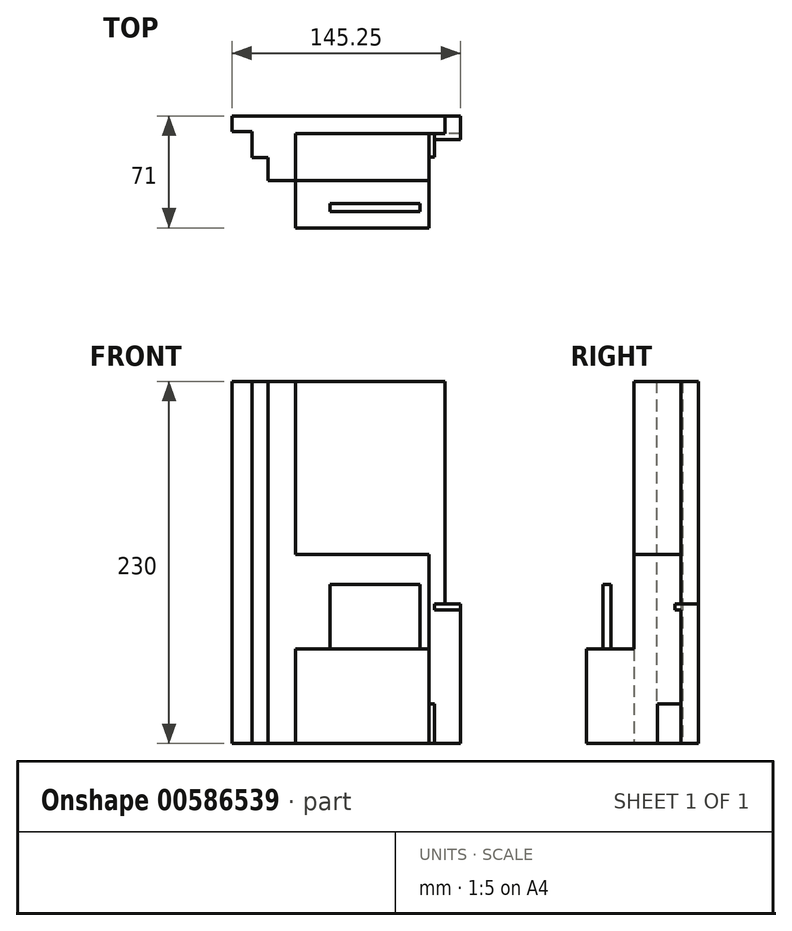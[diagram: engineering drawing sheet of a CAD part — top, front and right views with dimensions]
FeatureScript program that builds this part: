
annotation { "Feature Type Name" : "Feature", "Feature Type Description" : "" }
export const myFeature = defineFeature(function(context is Context, id is Id, definition is map)
    precondition{}
    {
        {
            var Q0;
            Q0=qCreatedBy(makeId("Top.planeOp"),FACE);
            var sketch = newSketch(context, id + "F0", { "sketchPlane" : qUnion([Q0])});
            skLineSegment(sketch, "E0", {"start": v(0, 0) * mm, "end": v(0, -30) * mm});
            skLineSegment(sketch, "E1", {"start": v(0, -30) * mm, "end": v(-17.5, -30) * mm});
            skLineSegment(sketch, "E2", {"start": v(-17.5, -30) * mm, "end": v(-17.5, -15.5) * mm});
            skLineSegment(sketch, "E3", {"start": v(-17.5, -15.5) * mm, "end": v(-27.5, -15.5) * mm});
            skLineSegment(sketch, "E4", {"start": v(-27.5, -15.5) * mm, "end": v(-27.5, 1) * mm});
            skLineSegment(sketch, "E5", {"start": v(-27.5, 1) * mm, "end": v(-40.25, 1) * mm});
            skLineSegment(sketch, "E6", {"start": v(-40.25, 1) * mm, "end": v(-40.25, 11) * mm});
            skLineSegment(sketch, "E7", {"start": v(-40.25, 11) * mm, "end": v(105, 11) * mm});
            skLineSegment(sketch, "E8", {"start": v(105, 11) * mm, "end": v(105, 0) * mm});
            skLineSegment(sketch, "E9", {"start": v(105, 0) * mm, "end": v(0, 0) * mm});
            skLineSegment(sketch, "E10", {"start": v(95, 0) * mm, "end": v(95, 11) * mm});
            skLineSegment(sketch, "E11", {"start": v(88.5, 0) * mm, "end": v(88.5, -4) * mm});
            skLineSegment(sketch, "E12", {"start": v(88.5, -4) * mm, "end": v(105, -4) * mm});
            skLineSegment(sketch, "E13", {"start": v(105, -4) * mm, "end": v(105, 0) * mm});
            skLineSegment(sketch, "E14", {"start": v(0, -15) * mm, "end": v(88.5, -15) * mm});
            skLineSegment(sketch, "E15", {"start": v(88.5, -15) * mm, "end": v(88.5, -4) * mm});
            skSolve(sketch);
        }
        {
            var Q0;
            Q0=makeQuery(id+"F0.imprint","IMPRINT",FACE,{"disambiguationData":[TD([[makeQuery(id+"F0.imprint","IMPRINT",EDGE,{"derivedFrom":sQuery(id+"F0.wireOp",EDGE,"E0")}),-1.0]])]});
            var Q1;
            {var subQ0=sQuery(id+"F0.wireOp",EDGE,"E8");Q1=makeQuery(id+"F0.imprint","IMPRINT",FACE,{"disambiguationData":[TD([[makeQuery(id+"F0.imprint","IMPRINT",EDGE,{"derivedFrom":subQ0}),-1.0]])]});}
            extrude(context, id + "F1", {"entities" : qUnion([Q0, Q1]), "depth" : 88.5 * mm, "offsetDistance" : 25 * mm});
        }
        {
            var Q0;
            {var subQ0=sQuery(id+"F0.wireOp",EDGE,"E11");Q0=makeQuery(id+"F0.imprint","IMPRINT",FACE,{"disambiguationData":[TD([[makeQuery(id+"F0.imprint","IMPRINT",EDGE,{"derivedFrom":subQ0}),1.0]])]});}
            var Q1;
            Q1=makeQuery(id+"F1.opExtrude","CAP_FACE",FACE,{"disambiguationData":[OSD([sQuery(id+"F0.wireOp",EDGE,"E0"),sQuery(id+"F0.wireOp",EDGE,"E1"),sQuery(id+"F0.wireOp",EDGE,"E2"),sQuery(id+"F0.wireOp",EDGE,"E3"),sQuery(id+"F0.wireOp",EDGE,"E4"),sQuery(id+"F0.wireOp",EDGE,"E5"),sQuery(id+"F0.wireOp",EDGE,"E6"),sQuery(id+"F0.wireOp",EDGE,"E7"),sQuery(id+"F0.wireOp",EDGE,"E8"),sQuery(id+"F0.wireOp",EDGE,"E9")])],"isStart":false});
            extrude(context, id + "F2", {"entities" : qUnion([Q0]), "operationType" : NewBodyOperationType.ADD, "endBound" : BoundingType.UP_TO_SURFACE, "depth" : 78.4 * mm, "endBoundEntityFace" : qUnion([Q1]), "offsetDistance" : 25 * mm, "hasSecondDirection" : true, "secondDirectionOppositeDirection" : false, "secondDirectionDepth" : 84.8 * mm});
        }
        {
            var Q0;
            {var subQ5=sQuery(id+"F0.wireOp",EDGE,"E0");Q0=makeQuery(id+"F0.imprint","IMPRINT",FACE,{"disambiguationData":[TD([[makeQuery(id+"F0.imprint","IMPRINT",EDGE,{"derivedFrom":subQ5}),-1.0]])]});}
            extrude(context, id + "F3", {"entities" : qUnion([Q0]), "operationType" : NewBodyOperationType.ADD, "depth" : 230 * mm, "offsetDistance" : 25 * mm});
        }
        {
            var Q0;
            {var subQ4=sQuery(id+"F0.wireOp",EDGE,"E11");Q0=makeQuery(id+"F0.imprint","IMPRINT",FACE,{"disambiguationData":[TD([[makeQuery(id+"F0.imprint","IMPRINT",EDGE,{"derivedFrom":subQ4}),-1.0]])]});}
            extrude(context, id + "F4", {"entities" : qUnion([Q0]), "operationType" : NewBodyOperationType.ADD, "depth" : 25 * mm, "offsetDistance" : 25 * mm});
        }
        {
            var Q0;
            Q0=qCreatedBy(makeId("Top.planeOp"),FACE);
            var sketch = newSketch(context, id + "F5", { "sketchPlane" : qUnion([Q0])});
            skLineSegment(sketch, "E16.bottom", {"start": v(0, 0) * mm, "end": v(85, 0) * mm});
            skLineSegment(sketch, "E16.top", {"start": v(0, -60) * mm, "end": v(85, -60) * mm});
            skLineSegment(sketch, "E16.left", {"start": v(0, 0) * mm, "end": v(0, -60) * mm});
            skLineSegment(sketch, "E16.right", {"start": v(85, 0) * mm, "end": v(85, -60) * mm});
            skLineSegment(sketch, "E17", {"start": v(85, -30) * mm, "end": v(0, -30) * mm});
            skSolve(sketch);
        }
        {
            var Q0;
            Q0 = qSketchRegion(id + "F5", true);
            extrude(context, id + "F6", {"entities" : qUnion([Q0]), "depth" : 60 * mm, "offsetDistance" : 25 * mm});
        }
        {
            var Q0;
            {var subQ0=sQuery(id+"F5.wireOp",EDGE,"E16.bottom");Q0=makeQuery(id+"F5.imprint","IMPRINT",FACE,{"disambiguationData":[TD([[makeQuery(id+"F5.imprint","IMPRINT",EDGE,{"derivedFrom":subQ0}),-1.0]])]});}
            extrude(context, id + "F7", {"entities" : qUnion([Q0]), "operationType" : NewBodyOperationType.ADD, "depth" : 120 * mm, "offsetDistance" : 25 * mm});
        }
        {
            var Q0;
            Q0=makeQuery(id+"F6.opExtrude","CAP_FACE",FACE,{"disambiguationData":[OSD([sQuery(id+"F5.wireOp",EDGE,"E16.bottom"),sQuery(id+"F5.wireOp",EDGE,"E16.top"),sQuery(id+"F5.wireOp",EDGE,"E16.left"),sQuery(id+"F5.wireOp",EDGE,"E16.right")])],"isStart":false});
            var sketch = newSketch(context, id + "F8", { "sketchPlane" : qUnion([Q0])});
            skLineSegment(sketch, "E18.bottom", {"start": v(22.04, -44.66) * mm, "end": v(79.04, -44.66) * mm});
            skLineSegment(sketch, "E18.top", {"start": v(22.04, -49.66) * mm, "end": v(79.04, -49.66) * mm});
            skLineSegment(sketch, "E18.left", {"start": v(22.04, -44.66) * mm, "end": v(22.04, -49.66) * mm});
            skLineSegment(sketch, "E18.right", {"start": v(79.04, -44.66) * mm, "end": v(79.04, -49.66) * mm});
            skSolve(sketch);
        }
        {
            var Q0;
            Q0 = qSketchRegion(id + "F8", true);
            extrude(context, id + "F9", {"entities" : qUnion([Q0]), "depth" : 41 * mm, "offsetDistance" : 25 * mm});
        }
    });
